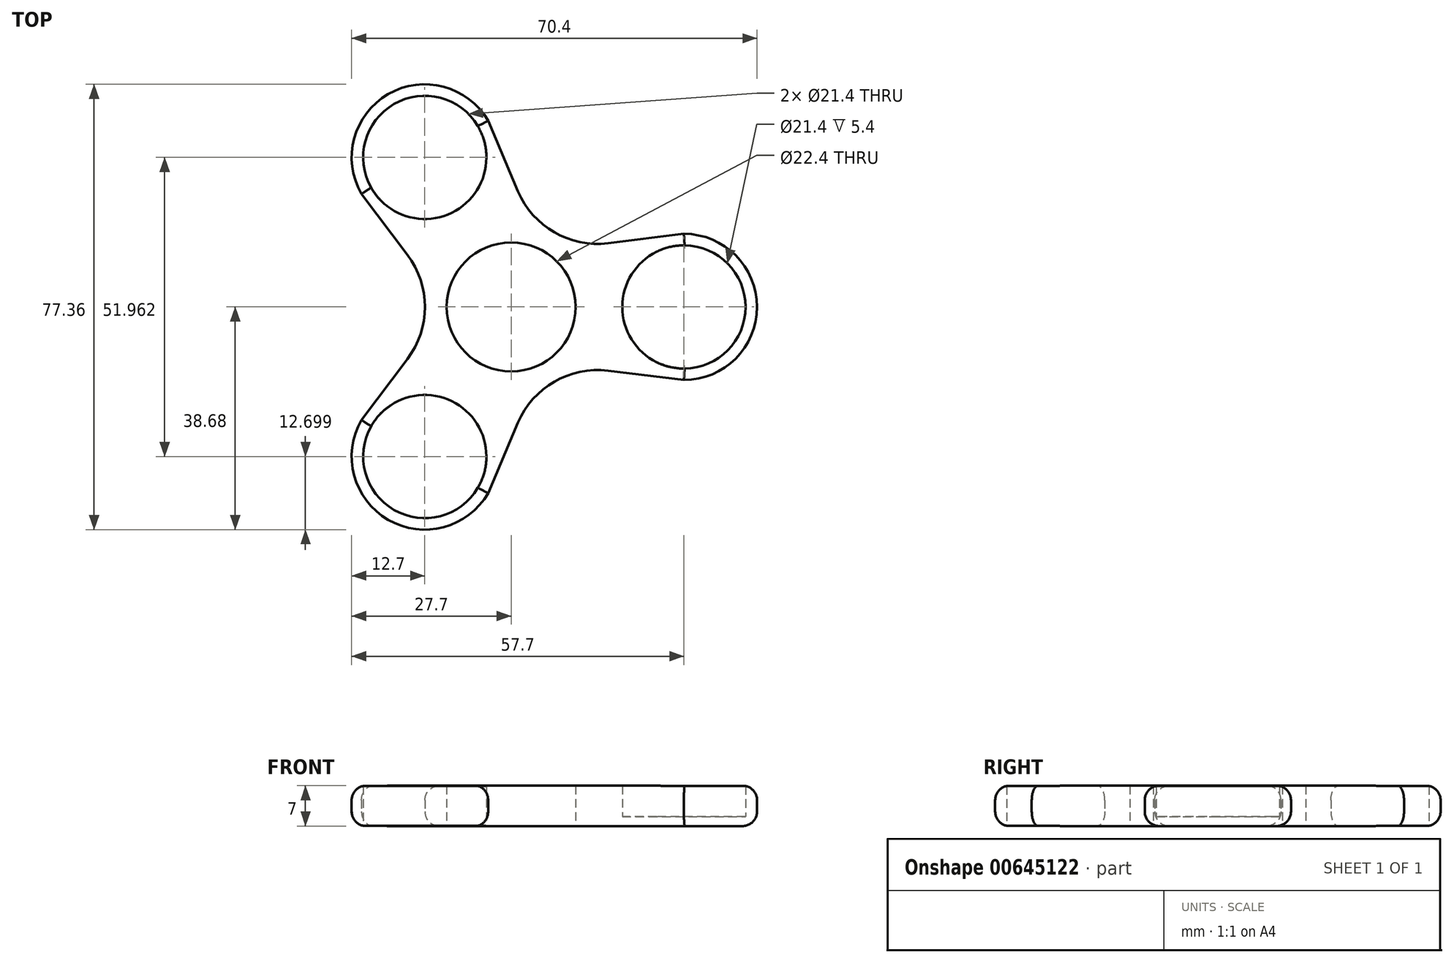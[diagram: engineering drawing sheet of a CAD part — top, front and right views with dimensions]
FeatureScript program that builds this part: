
annotation { "Feature Type Name" : "Feature", "Feature Type Description" : "" }
export const myFeature = defineFeature(function(context is Context, id is Id, definition is map)
    precondition{}
    {
        {
            var Q0;
            Q0=qCreatedBy(makeId("Top.planeOp"),FACE);
            var sketch = newSketch(context, id + "F0", { "sketchPlane" : qUnion([Q0])});
            skCircle(sketch, "E0", {"center": v(0, 0) * mm, "radius": 11.2 * mm});
            skLineSegment(sketch, "E1", {"start": v(0, 0) * mm, "end": v(55.1, 0) * mm, "construction": true});
            skLineSegment(sketch, "E2", {"start": v(0, 0) * mm, "end": v(-26.2, 45.38) * mm, "construction": true});
            skLineSegment(sketch, "E3", {"start": v(0, 0) * mm, "end": v(-25.98, -45) * mm, "construction": true});
            skCircle(sketch, "E4", {"center": v(30, 0) * mm, "radius": 10.7 * mm});
            skArc(sketch, "E5", {"start": v(26.92, -12.32) * mm, "mid": v(42.7, 0) * mm, "end": v(26.92, 12.32) * mm});
            skArc(sketch, "E6.MirrorC", {"start": v(-2.8, -29.48) * mm, "mid": v(-21.35, -36.98) * mm, "end": v(-24.13, -17.16) * mm});
            skCircle(sketch, "E7.MirrorC", {"center": v(-15, -25.98) * mm, "radius": 10.7 * mm});
            skArc(sketch, "E8.MirrorC", {"start": v(-24.13, 17.16) * mm, "mid": v(-21.35, 36.98) * mm, "end": v(-2.8, 29.48) * mm});
            skCircle(sketch, "E9.MirrorC", {"center": v(-15, 25.98) * mm, "radius": 10.7 * mm});
            skLineSegment(sketch, "E10", {"start": v(-26, 19.63) * mm, "end": v(-18, 9.03) * mm});
            skLineSegment(sketch, "E11.MirrorCS", {"start": v(-26, -19.63) * mm, "end": v(-18, -9.03) * mm});
            skPoint(sketch, "E12.visualSharp", {"position": v(-11.2, 0) * mm});
            skArc(sketch, "E12.filletArc", {"start": v(-18, -9.03) * mm, "mid": v(-14.98, 0) * mm, "end": v(-18, 9.03) * mm});
            skLineSegment(sketch, "E13.MirrorCS", {"start": v(-4, 32.33) * mm, "end": v(1.18, 20.1) * mm});
            skArc(sketch, "E14.MirrorCS", {"start": v(16.82, 11.08) * mm, "mid": v(7.5, 12.98) * mm, "end": v(1.18, 20.1) * mm});
            skLineSegment(sketch, "E15.MirrorCS", {"start": v(30, 12.7) * mm, "end": v(16.82, 11.08) * mm});
            skLineSegment(sketch, "E16.MirrorCS", {"start": v(30, -12.7) * mm, "end": v(16.82, -11.08) * mm});
            skArc(sketch, "E17.MirrorCS", {"start": v(1.18, -20.1) * mm, "mid": v(7.5, -12.98) * mm, "end": v(16.82, -11.08) * mm});
            skLineSegment(sketch, "E18.MirrorCS", {"start": v(-4, -32.33) * mm, "end": v(1.18, -20.1) * mm});
            skSolve(sketch);
        }
        {
            var Q0;
            Q0=makeQuery(id+"F0.imprint","IMPRINT",FACE,{"disambiguationData":[TD([[makeQuery(id+"F0.imprint","IMPRINT",EDGE,{"derivedFrom":sQuery(id+"F0.wireOp",EDGE,"E0")}),-1.0]])]});
            extrude(context, id + "F1", {"entities" : qUnion([Q0]), "depth" : 7 * mm, "offsetDistance" : 25 * mm});
        }
        {
            var Q0;
            Q0=makeQuery(id+"F0.imprint","IMPRINT",FACE,{"disambiguationData":[TD([[makeQuery(id+"F0.imprint","IMPRINT",EDGE,{"derivedFrom":sQuery(id+"F0.wireOp",EDGE,"E9.MirrorC")}),-1.0]])]});
            var Q1;
            Q1=makeQuery(id+"F0.imprint","IMPRINT",FACE,{"disambiguationData":[TD([[makeQuery(id+"F0.imprint","IMPRINT",EDGE,{"derivedFrom":sQuery(id+"F0.wireOp",EDGE,"E7.MirrorC")}),-1.0]])]});
            var Q2;
            Q2=makeQuery(id+"F0.imprint","IMPRINT",FACE,{"disambiguationData":[TD([[makeQuery(id+"F0.imprint","IMPRINT",EDGE,{"derivedFrom":sQuery(id+"F0.wireOp",EDGE,"E4")}),1.0]])]});
            extrude(context, id + "F2", {"entities" : qUnion([Q0, Q1, Q2]), "operationType" : NewBodyOperationType.ADD, "depth" : 1.6 * mm, "offsetDistance" : 25 * mm});
        }
        {
            var Q0;
            Q0=qCreatedBy(makeId("Top.planeOp"),FACE);
            cPlane(context, id + "F3", {"entities" : qUnion([Q0]), "cplaneType" : CPlaneType.OFFSET, "offset" : 7 * mm, "width" : 150 * mm, "height" : 150 * mm});
        }
        {
            var Q0;
            Q0=makeQuery(id+"F1.opExtrude","CAP_EDGE",EDGE,{"disambiguationData":[OSD([sQuery(id+"F0.wireOp",EDGE,"E17.MirrorCS")])],"isStart":false});
            var Q1;
            Q1=makeQuery(id+"F1.opExtrude","CAP_EDGE",EDGE,{"disambiguationData":[OSD([sQuery(id+"F0.wireOp",EDGE,"E14.MirrorCS")])],"isStart":false});
            var Q2;
            Q2=makeQuery(id+"F1.opExtrude","CAP_EDGE",EDGE,{"disambiguationData":[OSD([sQuery(id+"F0.wireOp",EDGE,"E12.filletArc")])],"isStart":false});
            var Q3;
            Q3=makeQuery(id+"F1.opExtrude","CAP_EDGE",EDGE,{"disambiguationData":[OSD([sQuery(id+"F0.wireOp",EDGE,"E6.MirrorC")])],"isStart":false});
            var Q4;
            Q4=makeQuery(id+"F1.opExtrude","CAP_EDGE",EDGE,{"disambiguationData":[OSD([sQuery(id+"F0.wireOp",EDGE,"E8.MirrorC")])],"isStart":false});
            var Q5;
            Q5=makeQuery(id+"F1.opExtrude","CAP_EDGE",EDGE,{"disambiguationData":[OSD([sQuery(id+"F0.wireOp",EDGE,"E5")])],"isStart":false});
            var Q6;
            Q6=makeQuery(id+"F1.opExtrude","CAP_EDGE",EDGE,{"disambiguationData":[OSD([sQuery(id+"F0.wireOp",EDGE,"E17.MirrorCS")])],"isStart":true});
            var Q7;
            Q7=makeQuery(id+"F1.opExtrude","CAP_EDGE",EDGE,{"disambiguationData":[OSD([sQuery(id+"F0.wireOp",EDGE,"E12.filletArc")])],"isStart":true});
            var Q8;
            Q8=makeQuery(id+"F1.opExtrude","CAP_EDGE",EDGE,{"disambiguationData":[OSD([sQuery(id+"F0.wireOp",EDGE,"E6.MirrorC")])],"isStart":true});
            var Q9;
            Q9=makeQuery(id+"F1.opExtrude","CAP_EDGE",EDGE,{"disambiguationData":[OSD([sQuery(id+"F0.wireOp",EDGE,"E15.MirrorCS")])],"isStart":true});
            var Q10;
            Q10=makeQuery(id+"F1.opExtrude","CAP_EDGE",EDGE,{"disambiguationData":[OSD([sQuery(id+"F0.wireOp",EDGE,"E5")])],"isStart":true});
            var Q11;
            Q11=makeQuery(id+"F1.opExtrude","CAP_EDGE",EDGE,{"disambiguationData":[OSD([sQuery(id+"F0.wireOp",EDGE,"E8.MirrorC")])],"isStart":true});
            fillet(context, id + "F4", {"entities" : qUnion([Q0, Q1, Q2, Q3, Q4, Q5, Q6, Q7, Q8, Q9, Q10, Q11]), "radius" : 2.5 * mm, "tangentPropagation" : true, "allowEdgeOverflow" : false});
        }
    });
